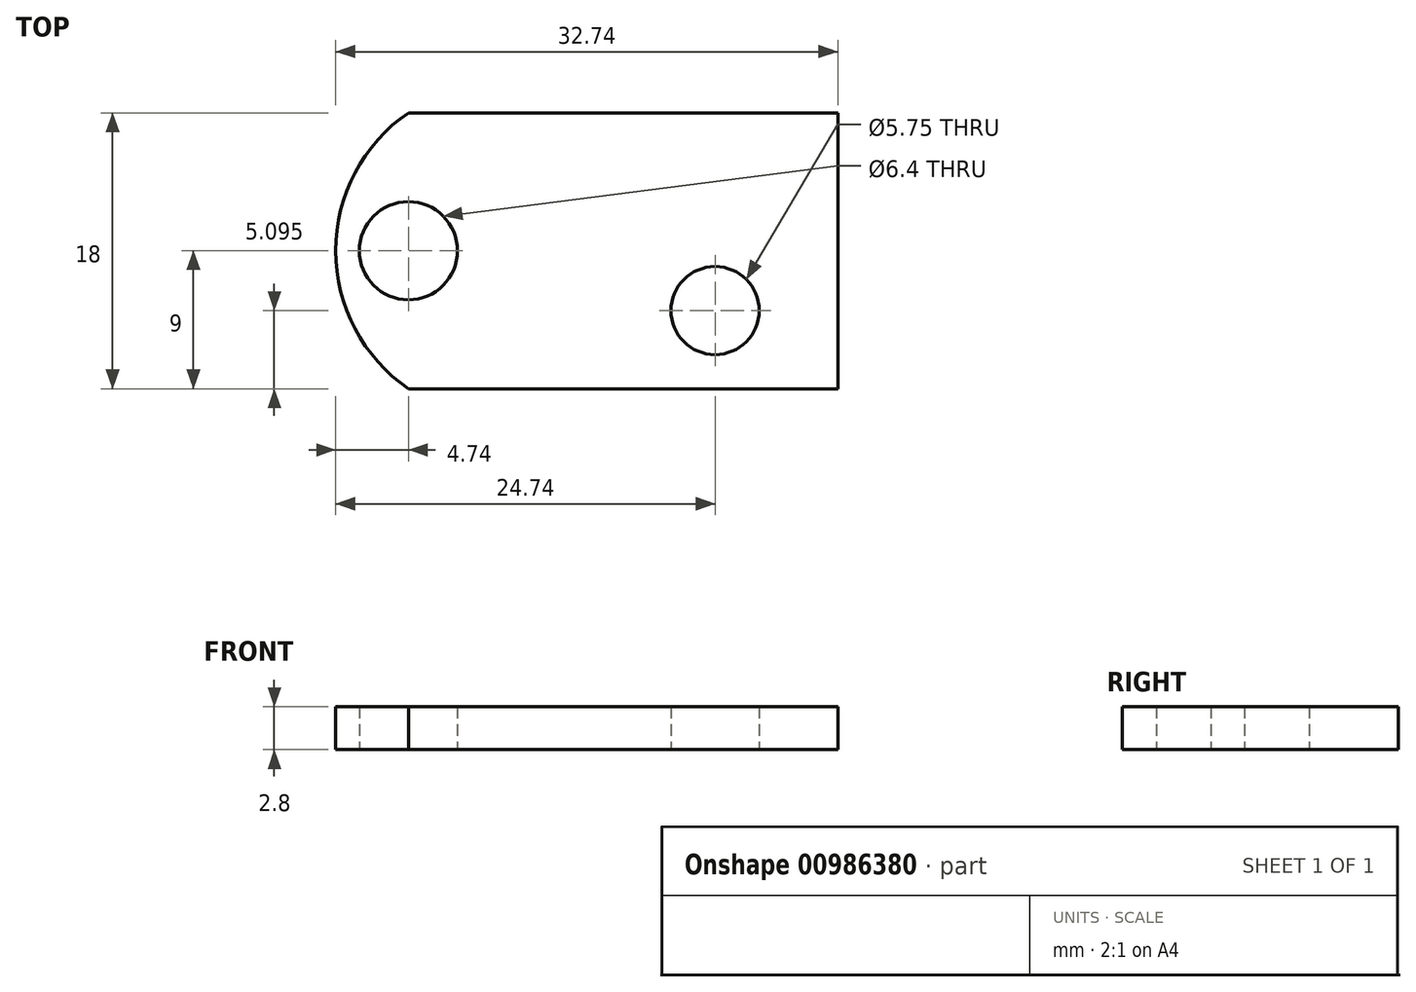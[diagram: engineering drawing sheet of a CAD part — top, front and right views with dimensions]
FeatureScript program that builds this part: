
annotation { "Feature Type Name" : "Feature", "Feature Type Description" : "" }
export const myFeature = defineFeature(function(context is Context, id is Id, definition is map)
    precondition{}
    {
        {
            var Q0;
            Q0=qCreatedBy(makeId("Top.planeOp"),FACE);
            var sketch = newSketch(context, id + "F0", { "sketchPlane" : qUnion([Q0])});
            skLineSegment(sketch, "E0.bottom", {"start": v(0, 0) * mm, "end": v(-28, 0) * mm});
            skLineSegment(sketch, "E0.top", {"start": v(0, -18) * mm, "end": v(-28, -18) * mm});
            skLineSegment(sketch, "E0.left", {"start": v(0, 0) * mm, "end": v(0, -18) * mm});
            skCircle(sketch, "E1", {"center": v(-8, -12.9) * mm, "radius": 2.88 * mm});
            skPoint(sketch, "E2", {"position": v(-8, -15.78) * mm});
            skLineSegment(sketch, "E3", {"start": v(-35, -9) * mm, "end": v(0, -9) * mm, "construction": true});
            skCircle(sketch, "E4", {"center": v(-28, -9) * mm, "radius": 3.2 * mm});
            skArc(sketch, "E5", {"start": v(-28, 0) * mm, "mid": v(-32.74, -9) * mm, "end": v(-28, -18) * mm});
            skPoint(sketch, "E6.orphan", {"position": v(-35, 0) * mm});
            skPoint(sketch, "E7.orphan", {"position": v(-35, -18) * mm});
            skSolve(sketch);
        }
        {
            var Q0;
            Q0=makeQuery(id+"F0.imprint","IMPRINT",FACE,{"disambiguationData":[TD([[makeQuery(id+"F0.imprint","IMPRINT",EDGE,{"derivedFrom":sQuery(id+"F0.wireOp",EDGE,"E0.bottom")}),1.0]])]});
            extrude(context, id + "F1", {"entities" : qUnion([Q0]), "depth" : 2.8 * mm, "offsetDistance" : 25 * mm});
        }
    });
